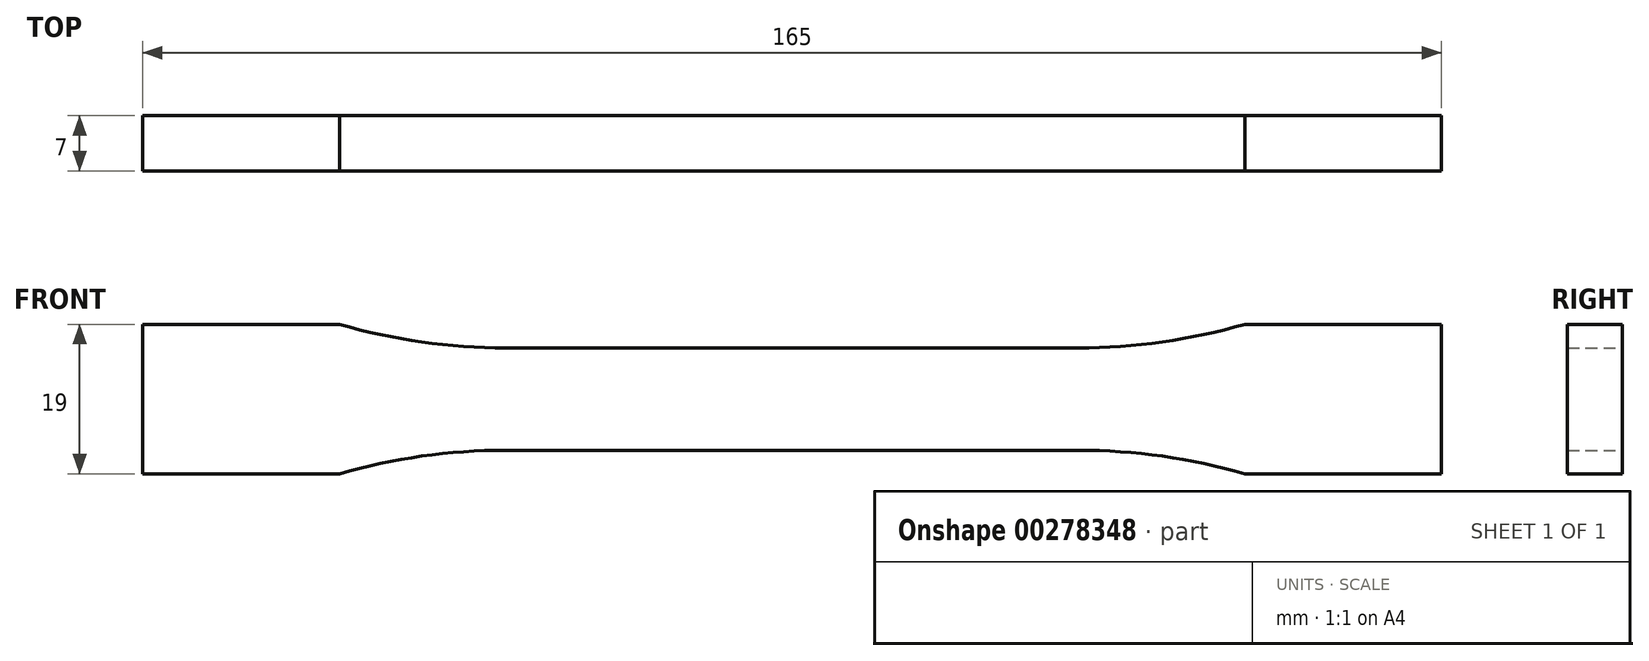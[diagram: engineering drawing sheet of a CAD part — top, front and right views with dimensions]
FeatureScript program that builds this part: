
annotation { "Feature Type Name" : "Feature", "Feature Type Description" : "" }
export const myFeature = defineFeature(function(context is Context, id is Id, definition is map)
    precondition{}
    {
        {
            var Q0;
            Q0=qCreatedBy(makeId("Front.planeOp"),FACE);
            var sketch = newSketch(context, id + "F0", { "sketchPlane" : qUnion([Q0])});
            skLineSegment(sketch, "E0", {"start": v(0, 6.5) * mm, "end": v(36.36, 6.5) * mm});
            skArc(sketch, "E1", {"start": v(36.36, 6.5) * mm, "mid": v(47.03, 7.25) * mm, "end": v(57.5, 9.5) * mm});
            skLineSegment(sketch, "E2", {"start": v(57.5, 9.5) * mm, "end": v(82.5, 9.5) * mm});
            skLineSegment(sketch, "E3.MirrorCS", {"start": v(57.5, -9.5) * mm, "end": v(82.5, -9.5) * mm});
            skLineSegment(sketch, "E4.MirrorCS", {"start": v(0, -6.5) * mm, "end": v(36.36, -6.5) * mm});
            skArc(sketch, "E5.MirrorCS", {"start": v(36.36, -6.5) * mm, "mid": v(47.03, -7.25) * mm, "end": v(57.5, -9.5) * mm});
            skArc(sketch, "E6.MirrorCS", {"start": v(-36.36, -6.5) * mm, "mid": v(-47.03, -7.25) * mm, "end": v(-57.5, -9.5) * mm});
            skLineSegment(sketch, "E7.MirrorCS", {"start": v(0, 6.5) * mm, "end": v(-36.36, 6.5) * mm});
            skArc(sketch, "E8.MirrorCS", {"start": v(-36.36, 6.5) * mm, "mid": v(-47.03, 7.25) * mm, "end": v(-57.5, 9.5) * mm});
            skLineSegment(sketch, "E9.MirrorCS", {"start": v(0, -6.5) * mm, "end": v(-36.36, -6.5) * mm});
            skLineSegment(sketch, "E10.MirrorCS", {"start": v(-57.5, 9.5) * mm, "end": v(-82.5, 9.5) * mm});
            skLineSegment(sketch, "E11.MirrorCS", {"start": v(-57.5, -9.5) * mm, "end": v(-82.5, -9.5) * mm});
            skLineSegment(sketch, "E12", {"start": v(-82.5, -9.5) * mm, "end": v(-82.5, 9.5) * mm});
            skLineSegment(sketch, "E13", {"start": v(82.5, -9.5) * mm, "end": v(82.5, 9.5) * mm});
            skSolve(sketch);
        }
        {
            var Q0;
            Q0 = qSketchRegion(id + "F0", true);
            extrude(context, id + "F1", {"entities" : qUnion([Q0]), "endBound" : BoundingType.SYMMETRIC, "depth" : 7 * mm});
        }
    });
